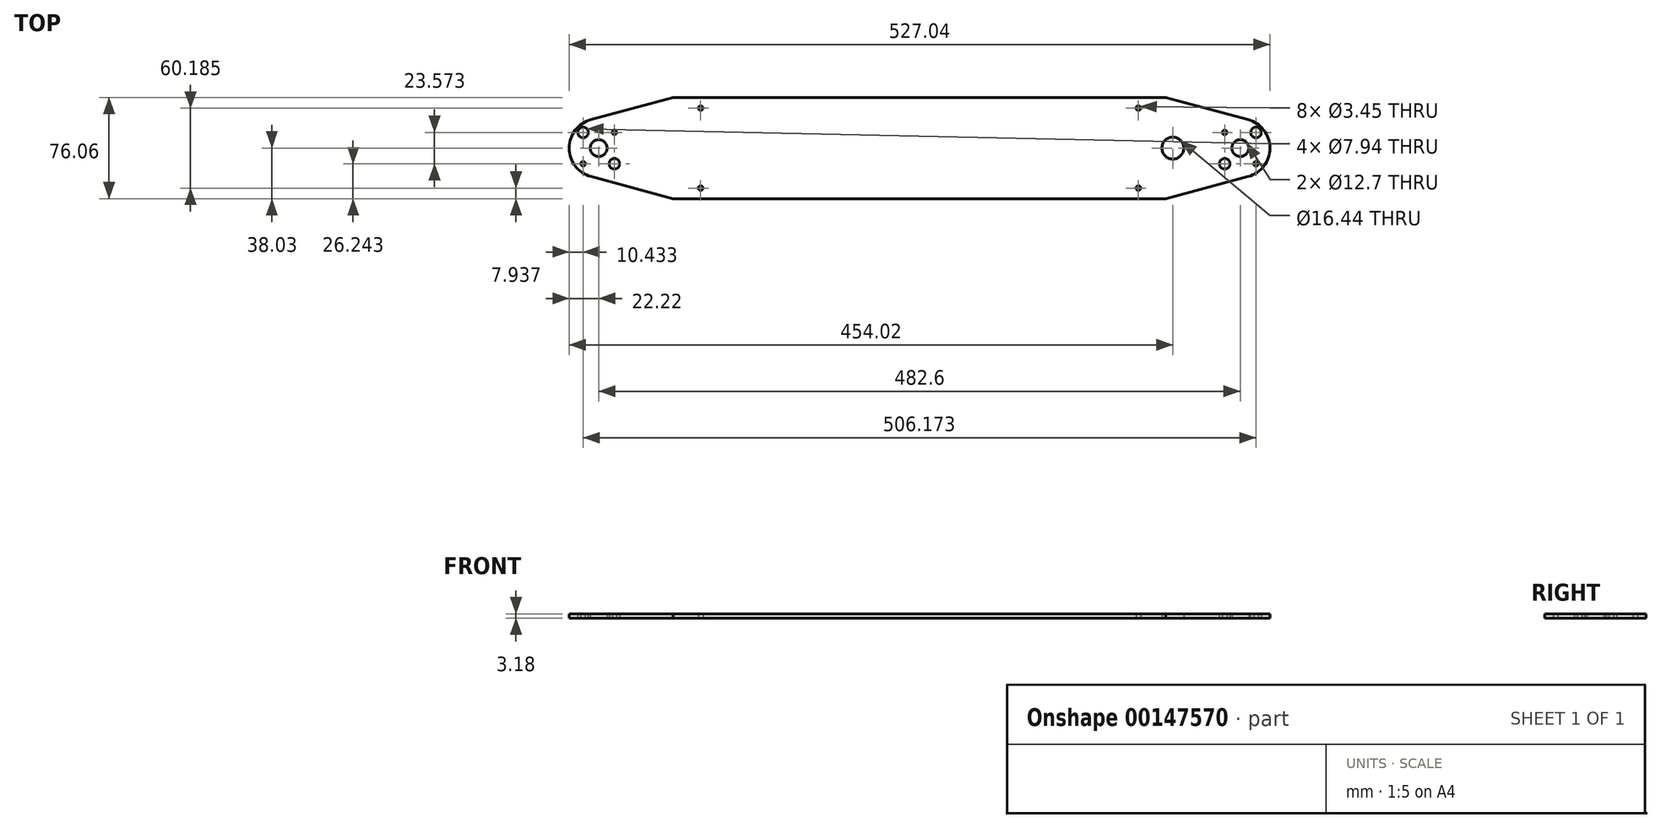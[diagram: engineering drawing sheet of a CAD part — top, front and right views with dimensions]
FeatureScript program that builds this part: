
annotation { "Feature Type Name" : "Feature", "Feature Type Description" : "" }
export const myFeature = defineFeature(function(context is Context, id is Id, definition is map)
    precondition{}
    {
        {
            var Q0;
            Q0=qCreatedBy(makeId("Top.planeOp"),FACE);
            var sketch = newSketch(context, id + "F0", { "sketchPlane" : qUnion([Q0])});
            skPoint(sketch, "E0.rect.middle", {"position": v(0, 0) * mm});
            skCircle(sketch, "E1", {"center": v(0, 0) * mm, "radius": 11.11 * mm, "construction": true});
            skLineSegment(sketch, "E2.bottom", {"start": v(11.79, 11.79) * mm, "end": v(-11.79, 11.79) * mm, "construction": true});
            skLineSegment(sketch, "E2.left", {"start": v(11.79, 11.79) * mm, "end": v(11.79, -11.79) * mm, "construction": true});
            skLineSegment(sketch, "E2.right", {"start": v(-11.79, 11.79) * mm, "end": v(-11.79, -11.79) * mm, "construction": true});
            skCircle(sketch, "E3", {"center": v(11.79, 11.79) * mm, "radius": 5.56 * mm, "construction": true});
            skCircle(sketch, "E4", {"center": v(-11.79, 11.79) * mm, "radius": 1.73 * mm});
            skCircle(sketch, "E5", {"center": v(11.79, 11.79) * mm, "radius": 3.97 * mm});
            skCircle(sketch, "E6", {"center": v(11.79, -11.79) * mm, "radius": 1.73 * mm});
            skCircle(sketch, "E7", {"center": v(-11.79, -11.79) * mm, "radius": 3.97 * mm});
            skArc(sketch, "E8", {"start": v(-488.35, 21.47) * mm, "mid": v(-504.83, 0) * mm, "end": v(-488.35, -21.47) * mm});
            skLineSegment(sketch, "E9.bottom", {"start": v(-494.39, 11.79) * mm, "end": v(-470.81, 11.79) * mm, "construction": true});
            skLineSegment(sketch, "E9.top", {"start": v(-494.39, -11.79) * mm, "end": v(-470.81, -11.79) * mm, "construction": true});
            skLineSegment(sketch, "E9.left", {"start": v(-494.39, 11.79) * mm, "end": v(-494.39, -11.79) * mm, "construction": true});
            skLineSegment(sketch, "E9.right", {"start": v(-470.81, 11.79) * mm, "end": v(-470.81, -11.79) * mm, "construction": true});
            skCircle(sketch, "E10", {"center": v(-470.81, 11.79) * mm, "radius": 1.73 * mm});
            skCircle(sketch, "E11", {"center": v(-482.6, 0) * mm, "radius": 6.35 * mm});
            skCircle(sketch, "E12", {"center": v(-494.39, 11.79) * mm, "radius": 3.97 * mm});
            skCircle(sketch, "E13", {"center": v(-494.39, -11.79) * mm, "radius": 1.73 * mm});
            skCircle(sketch, "E14", {"center": v(-470.81, -11.79) * mm, "radius": 3.97 * mm});
            skLineSegment(sketch, "E15", {"start": v(0, 0) * mm, "end": v(-482.6, 0) * mm, "construction": true});
            skLineSegment(sketch, "E16", {"start": v(-488.35, -21.47) * mm, "end": v(-426.54, -38.03) * mm});
            skLineSegment(sketch, "E17", {"start": v(-488.35, 21.47) * mm, "end": v(-426.54, 38.03) * mm});
            skLineSegment(sketch, "E18", {"start": v(-420.2, -34.86) * mm, "end": v(-62.4, -34.86) * mm, "construction": true});
            skLineSegment(sketch, "E19", {"start": v(-420.2, 34.86) * mm, "end": v(-62.4, 34.86) * mm, "construction": true});
            skLineSegment(sketch, "E20", {"start": v(-420.2, 38.03) * mm, "end": v(-420.2, 34.86) * mm, "construction": true});
            skLineSegment(sketch, "E21", {"start": v(-420.2, 38.03) * mm, "end": v(-426.54, 38.03) * mm});
            skLineSegment(sketch, "E22", {"start": v(-420.2, -34.86) * mm, "end": v(-420.2, -38.03) * mm, "construction": true});
            skLineSegment(sketch, "E23", {"start": v(-420.2, -38.03) * mm, "end": v(-426.54, -38.03) * mm});
            skLineSegment(sketch, "E24", {"start": v(-62.4, -34.86) * mm, "end": v(-62.4, -38.03) * mm, "construction": true});
            skLineSegment(sketch, "E25", {"start": v(-62.4, -38.03) * mm, "end": v(-56.06, -38.03) * mm});
            skLineSegment(sketch, "E26", {"start": v(-62.4, 34.86) * mm, "end": v(-62.4, 38.03) * mm, "construction": true});
            skLineSegment(sketch, "E27", {"start": v(-62.4, 38.03) * mm, "end": v(-56.06, 38.03) * mm});
            skLineSegment(sketch, "E28", {"start": v(-56.06, -38.03) * mm, "end": v(5.75, -21.47) * mm});
            skLineSegment(sketch, "E29", {"start": v(5.75, 21.47) * mm, "end": v(-56.06, 38.03) * mm});
            skArc(sketch, "E30", {"start": v(5.75, -21.47) * mm, "mid": v(22.23, 0) * mm, "end": v(5.75, 21.47) * mm});
            skLineSegment(sketch, "E31", {"start": v(-420.2, 34.86) * mm, "end": v(-420.2, 30.1) * mm, "construction": true});
            skLineSegment(sketch, "E32", {"start": v(-420.2, 30.1) * mm, "end": v(-405.9, 30.1) * mm, "construction": true});
            skLineSegment(sketch, "E33", {"start": v(-420.2, -34.86) * mm, "end": v(-420.2, -30.1) * mm, "construction": true});
            skLineSegment(sketch, "E34", {"start": v(-420.2, -30.1) * mm, "end": v(-405.9, -30.1) * mm, "construction": true});
            skLineSegment(sketch, "E35", {"start": v(-62.4, -34.86) * mm, "end": v(-62.4, -30.1) * mm, "construction": true});
            skLineSegment(sketch, "E36", {"start": v(-62.4, -30.1) * mm, "end": v(-76.7, -30.1) * mm, "construction": true});
            skLineSegment(sketch, "E37", {"start": v(-62.4, 34.86) * mm, "end": v(-62.4, 30.1) * mm, "construction": true});
            skLineSegment(sketch, "E38", {"start": v(-62.4, 30.1) * mm, "end": v(-76.7, 30.1) * mm, "construction": true});
            skCircle(sketch, "E39", {"center": v(-405.9, 30.1) * mm, "radius": 1.73 * mm});
            skCircle(sketch, "E40", {"center": v(-76.7, 30.1) * mm, "radius": 1.73 * mm});
            skCircle(sketch, "E41", {"center": v(-76.7, -30.1) * mm, "radius": 1.73 * mm});
            skCircle(sketch, "E42", {"center": v(-405.9, -30.1) * mm, "radius": 1.73 * mm});
            skLineSegment(sketch, "E43", {"start": v(-11.79, -11.79) * mm, "end": v(11.79, -11.79) * mm, "construction": true});
            skLineSegment(sketch, "E44", {"start": v(-241.3, -34.86) * mm, "end": v(-241.3, 0) * mm, "construction": true});
            skLineSegment(sketch, "E45", {"start": v(-241.3, 0) * mm, "end": v(-241.3, 34.86) * mm, "construction": true});
            skCircle(sketch, "E46", {"center": v(-50.8, 0) * mm, "radius": 8.22 * mm});
            skCircle(sketch, "E47", {"center": v(0, 0) * mm, "radius": 6.35 * mm});
            skCircle(sketch, "E48", {"center": v(-494.39, 11.79) * mm, "radius": 5.56 * mm, "construction": true});
            skLineSegment(sketch, "E49", {"start": v(-488.35, 21.47) * mm, "end": v(-457.45, 21.47) * mm, "construction": true});
            skLineSegment(sketch, "E50", {"start": v(-457.45, 21.47) * mm, "end": v(-457.45, 29.75) * mm, "construction": true});
            skLineSegment(sketch, "E51", {"start": v(-420.2, 38.03) * mm, "end": v(-62.4, 38.03) * mm});
            skLineSegment(sketch, "E52", {"start": v(-62.4, -38.03) * mm, "end": v(-420.2, -38.03) * mm});
            skSolve(sketch);
        }
        {
            var Q0;
            Q0=qSketchRegion(id+"F0",true);
            extrude(context, id + "F1", {"entities" : qUnion([Q0]), "depth" : 3.17 * mm});
        }
    });
